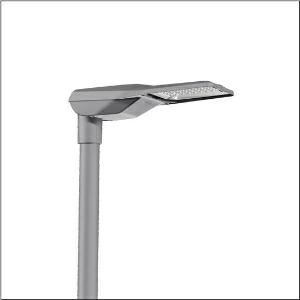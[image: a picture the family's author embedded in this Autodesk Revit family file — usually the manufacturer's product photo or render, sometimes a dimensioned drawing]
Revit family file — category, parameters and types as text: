
# Revit family: streetlight_sl_21_iq_mini___st0_8a_5xe2c31d08jb_69b6
name_source: partatom
category: Lighting Fixtures
units: mm (PartAtom-declared; Revit-internal decimal feet)

## family parameters
Cut with Voids When Loaded = No
Host = Face
Light Source = No
Part Type = Normal
Room Calculation Point = No
Round Connector Dimension = Use Diameter
Shared = No

## types (1)
- --- (1 x LED, 10820 lm, 71.6 W, 3000K)
    Apparent Load = 72 VA
    CIE Flux Codes = 41 75 97 100 100
    Color Rendering = 70
    Color Temperature = 3000K
    Default Elevation = 1800 mm
    Description = Streetlight SL 21 iQ mini, mast luminaire, primary light control with lens, of PMMA, primary optical cover: cover, of toughened safety glass, transparent, light distribution: ST0.8a, light emission: direct distribution, primary light characteristic: asymmetric, installation type: post-top, side-entry, LED, High Power LED, rated luminous flux: 10.820lm, luminous efficacy: 151lm/W, light colour: 730, colour temperature: 3000K, control gear: iQ-Comfort, control: Auto-Match, Temp-Guard, Lumen-Switch, Night-Set, Smart-Wire, Light-Fading, Desk-Remote (wireless, voltage-free reading and setting of iQ features in the workshop via application-optimized NFC function/RFID function), optimised constant luminous flux control (CLO 2.0), pre-setting: linear dimming characteristic, mains connection: 220..240V, AC, 50/60Hz, start of lifetime: 72W, end of service life: 75W, reduction: 33W, luminaire housing, of diecast aluminium, powder-coated, Siteco® metallic grey (DB 702S), corrosivity category C5 high according to DIN EN ISO 12944, please order mast flange separately, inclination adjustable: 0°, 5°, 10°, 15°, sealing non-destructively replaceable, multi-level sealing system, length: 628mm, width: 235mm, height: 110mm, mast flange for spigot size: 42mm (side-entry): 5XC10008XM4, 60/48mm (side-entry/post-top): 5XC10108XM2, 76/60mm (side-entry/post-top): 5XC10108XM1, mounting height: 4..8m, protection rating (complete): IP66, insulation class (complete): insulation class II (safety insulation), certification: CE, ENEC, ENEC+, VDE, impact resistance: IK10, permissible operating ambient temperature for outdoor applications: -40..+50°C, standard-compliant lighting for roads and squares, packaging unit: 1 piece

Light Distribution: ST0.8a
    Height = 110 mm
    Lamp = 1 x LED
    Lamp Light Flux = 10820 lm
    Lamp Power = 71.6 W
    Lamp count = 1
    Length = 625 mm
    Luminous efficacy = 151 lm/W
    Manufacturer = Siteco
    ModVariant = No
    Model = 5XE2C31D08JB
    Number of Poles = 1
    OnlyDefault = Yes
    Power Factor = 1
    Product Name = Streetlight SL 21 iQ mini | ST0.8a
    Product group = mast luminaire | pylon top
    ProductGroupID = 6100
    Protection Class = Protection class II
    Protection Degree = IP 66
    RLX_Detail_Level = 1
    RLX_Emergency_Light_Flux = 0 lm
    RLX_Emergency_Type = 0
    RLX_Emergency_Type_DB = No
    RlxData = <blob elided: 26357 chars, md5=cca3bf26>
    Socket = socket
    Standby Power = 0 W
    System Light Flux = 10820 lm
    System Power = 72 W
    Type Comments = factory setting: luminous flux: 100 % | dim-lin: 254 | 746 mA
    Type Image = l_1003519.jpg
    URL = http://relux.com
    VarID = @adj_172565
    Voltage = 0 V
    Weight = 0.00 kg
    Width = 234 mm

## geometry (parser evidence)
native form markers: Blend x4, Sweep x12
no freeform markers — native parametric forms only
